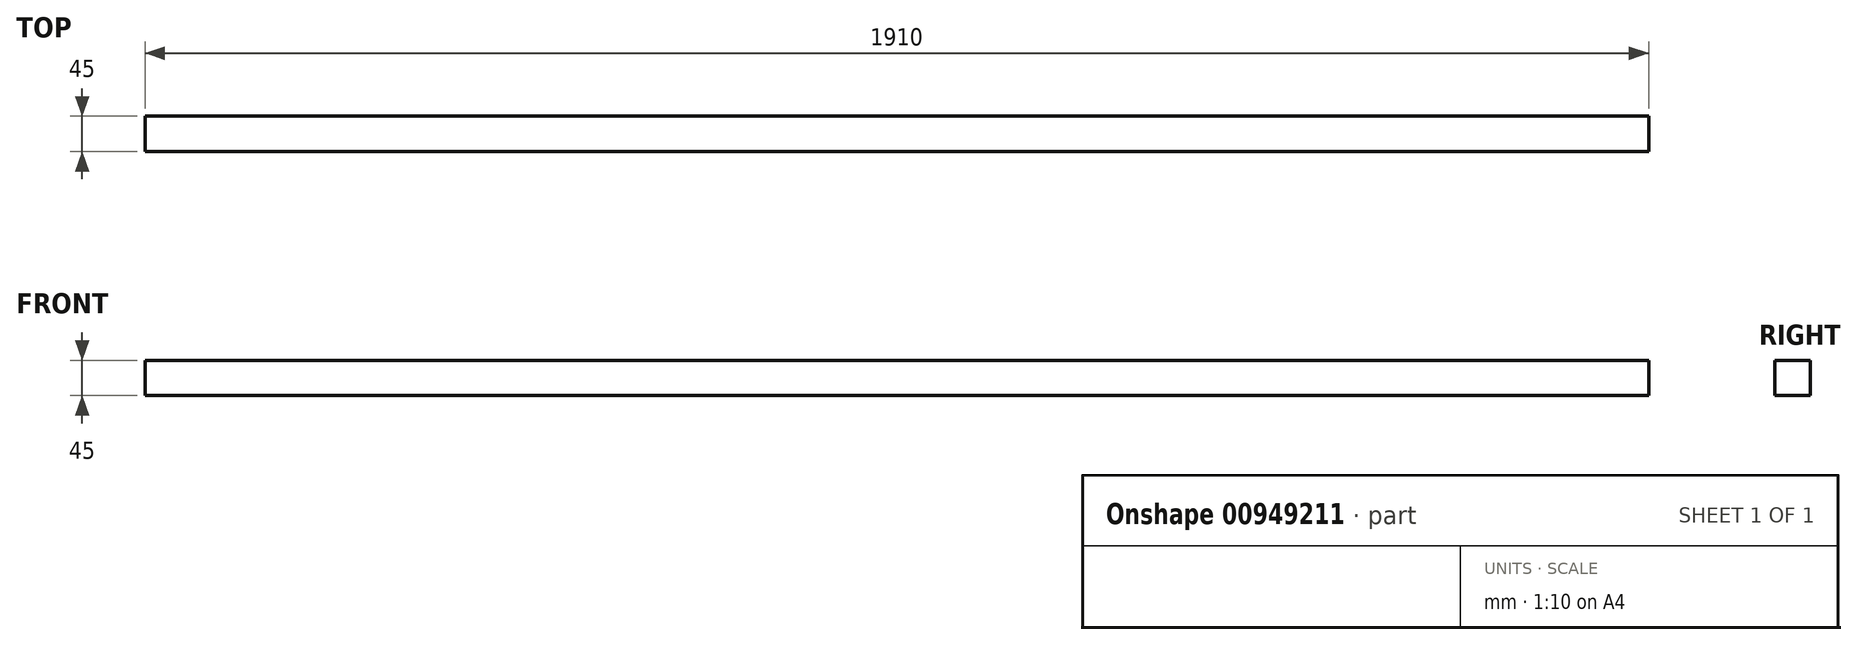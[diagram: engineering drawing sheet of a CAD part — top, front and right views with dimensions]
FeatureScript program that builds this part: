
annotation { "Feature Type Name" : "Feature", "Feature Type Description" : "" }
export const myFeature = defineFeature(function(context is Context, id is Id, definition is map)
    precondition{}
    {
        {
            var Q0;
            Q0=qCreatedBy(makeId("Front.planeOp"),FACE);
            var sketch = newSketch(context, id + "F0", { "sketchPlane" : qUnion([Q0])});
            skLineSegment(sketch, "E0.bottom", {"start": v(955, -22.5) * mm, "end": v(-955, -22.5) * mm});
            skLineSegment(sketch, "E0.top", {"start": v(955, 22.5) * mm, "end": v(-955, 22.5) * mm});
            skLineSegment(sketch, "E0.left", {"start": v(955, -22.5) * mm, "end": v(955, 22.5) * mm});
            skLineSegment(sketch, "E0.right", {"start": v(-955, -22.5) * mm, "end": v(-955, 22.5) * mm});
            skPoint(sketch, "E0.middle", {"position": v(0, 0) * mm});
            skSolve(sketch);
        }
        {
            var Q0;
            Q0 = qSketchRegion(id + "F0", true);
            extrude(context, id + "F1", {"entities" : qUnion([Q0]), "depth" : 45 * mm, "offsetDistance" : 25 * mm});
        }
    });
